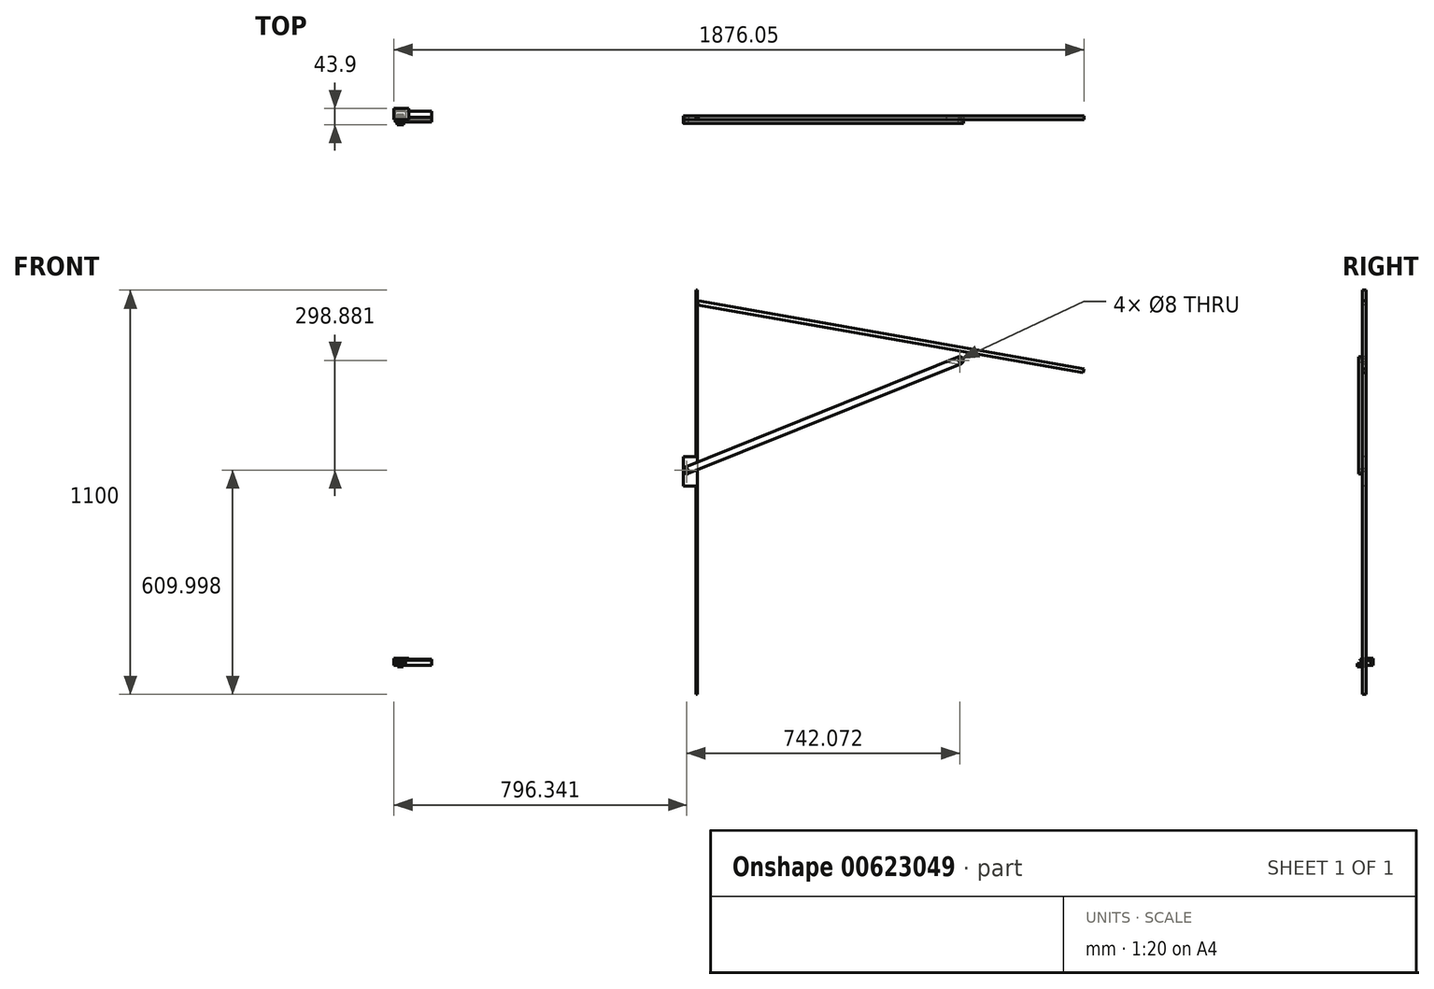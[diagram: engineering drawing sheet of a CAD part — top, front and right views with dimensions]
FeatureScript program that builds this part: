
annotation { "Feature Type Name" : "Feature", "Feature Type Description" : "" }
export const myFeature = defineFeature(function(context is Context, id is Id, definition is map)
    precondition{}
    {
        {
            var Q0;
            Q0=qCreatedBy(makeId("Front.planeOp"),FACE);
            var sketch = newSketch(context, id + "F0", { "sketchPlane" : qUnion([Q0])});
            skLineSegment(sketch, "E0.bottom", {"start": v(-1171.87, 12) * mm, "end": v(-1146.87, 12) * mm});
            skLineSegment(sketch, "E0.top", {"start": v(-1171.87, 0) * mm, "end": v(-1146.87, 0) * mm});
            skLineSegment(sketch, "E0.left", {"start": v(-1171.87, 12) * mm, "end": v(-1171.87, 0) * mm});
            skLineSegment(sketch, "E0.right", {"start": v(-1146.87, 12) * mm, "end": v(-1146.87, 0) * mm});
            skLineSegment(sketch, "E1.bottom", {"start": v(-1104.3, 0) * mm, "end": v(-1101.3, 0) * mm});
            skLineSegment(sketch, "E1.left", {"start": v(-1104.3, 0) * mm, "end": v(-1104.3, 20) * mm});
            skLineSegment(sketch, "E1.right", {"start": v(-1101.3, 0) * mm, "end": v(-1101.3, 17) * mm});
            skLineSegment(sketch, "E2.bottom", {"start": v(-1104.3, 20) * mm, "end": v(-1064.3, 20) * mm});
            skLineSegment(sketch, "E2.top", {"start": v(-1101.3, 17) * mm, "end": v(-1064.3, 17) * mm});
            skLineSegment(sketch, "E2.right", {"start": v(-1064.3, 20) * mm, "end": v(-1064.3, 17) * mm});
            skLineSegment(sketch, "E3.bottom", {"start": v(-1101.3, 17) * mm, "end": v(-1001.3, 17) * mm});
            skLineSegment(sketch, "E3.top", {"start": v(-1073.3, 0) * mm, "end": v(-1001.3, 0) * mm});
            skLineSegment(sketch, "E3.left", {"start": v(-1101.3, 17) * mm, "end": v(-1101.3, 9) * mm});
            skLineSegment(sketch, "E3.right", {"start": v(-1001.3, 17) * mm, "end": v(-1001.3, 0) * mm});
            skLineSegment(sketch, "E4", {"start": v(-1101.3, 15) * mm, "end": v(-1001.3, 15) * mm});
            skLineSegment(sketch, "E5", {"start": v(-1073.3, 0) * mm, "end": v(-1073.3, 9) * mm});
            skLineSegment(sketch, "E6", {"start": v(-1073.3, 9) * mm, "end": v(-1101.3, 9) * mm});
            skLineSegment(sketch, "E7.bottom", {"start": v(-1099.58, 0) * mm, "end": v(-1092.08, 0) * mm});
            skLineSegment(sketch, "E7.top", {"start": v(-1099.58, 9) * mm, "end": v(-1074.58, 9) * mm});
            skLineSegment(sketch, "E7.left", {"start": v(-1099.58, 0) * mm, "end": v(-1099.58, 9) * mm});
            skLineSegment(sketch, "E7.right", {"start": v(-1074.58, 0) * mm, "end": v(-1074.58, 9) * mm});
            skLineSegment(sketch, "E8", {"start": v(-1092.08, 0) * mm, "end": v(-1092.08, 2) * mm});
            skLineSegment(sketch, "E9", {"start": v(-1092.08, 2) * mm, "end": v(-1097.58, 2) * mm});
            skLineSegment(sketch, "E10", {"start": v(-1097.58, 2) * mm, "end": v(-1097.58, 7) * mm});
            skLineSegment(sketch, "E11", {"start": v(-1097.58, 7) * mm, "end": v(-1076.58, 7) * mm});
            skLineSegment(sketch, "E12", {"start": v(-1076.58, 7) * mm, "end": v(-1076.58, 2) * mm});
            skLineSegment(sketch, "E13", {"start": v(-1076.58, 2) * mm, "end": v(-1082.08, 2) * mm});
            skLineSegment(sketch, "E14", {"start": v(-1082.08, 2) * mm, "end": v(-1082.08, 0) * mm});
            skLineSegment(sketch, "E15.trimOffspring", {"start": v(-1082.08, 0) * mm, "end": v(-1074.58, 0) * mm});
            skLineSegment(sketch, "E16", {"start": v(-1094.68, -0.73) * mm, "end": v(-1094.68, -2.73) * mm});
            skLineSegment(sketch, "E17", {"start": v(-1094.68, -2.73) * mm, "end": v(-1079.68, -2.73) * mm});
            skLineSegment(sketch, "E18", {"start": v(-1079.68, -2.73) * mm, "end": v(-1079.68, -0.73) * mm});
            skLineSegment(sketch, "E19", {"start": v(-1079.68, -0.73) * mm, "end": v(-1083.18, -0.73) * mm});
            skLineSegment(sketch, "E20", {"start": v(-1083.18, -0.73) * mm, "end": v(-1083.18, 3.35) * mm});
            skLineSegment(sketch, "E21", {"start": v(-1083.18, 3.35) * mm, "end": v(-1077.87, 3.35) * mm});
            skLineSegment(sketch, "E22", {"start": v(-1077.87, 3.35) * mm, "end": v(-1077.87, 5.32) * mm});
            skLineSegment(sketch, "E23", {"start": v(-1077.87, 5.32) * mm, "end": v(-1096.5, 5.32) * mm});
            skLineSegment(sketch, "E24", {"start": v(-1096.5, 5.32) * mm, "end": v(-1096.5, 3.35) * mm});
            skLineSegment(sketch, "E25", {"start": v(-1096.5, 3.35) * mm, "end": v(-1091.18, 3.35) * mm});
            skLineSegment(sketch, "E26", {"start": v(-1091.18, 3.35) * mm, "end": v(-1091.18, -0.73) * mm});
            skLineSegment(sketch, "E27", {"start": v(-1091.18, -0.73) * mm, "end": v(-1094.68, -0.73) * mm});
            skLineSegment(sketch, "E28.bottom", {"start": v(-539.23, 1032.76) * mm, "end": v(-535.23, 1032.76) * mm});
            skLineSegment(sketch, "E28.top", {"start": v(-539.23, -67.24) * mm, "end": v(-535.23, -67.24) * mm});
            skLineSegment(sketch, "E28.left", {"start": v(-539.23, 1032.76) * mm, "end": v(-539.23, -67.24) * mm});
            skLineSegment(sketch, "E28.right", {"start": v(-535.23, 1032.76) * mm, "end": v(-535.23, -67.24) * mm});
            skLineSegment(sketch, "E29.left", {"start": v(-533.23, -72.18) * mm, "end": v(-533.23, 992.82) * mm});
            skLineSegment(sketch, "E29.right", {"start": v(-513.23, -72.18) * mm, "end": v(-513.23, 992.82) * mm});
            skLineSegment(sketch, "E30", {"start": v(-533.23, 992.82) * mm, "end": v(-513.23, 992.82) * mm});
            skLineSegment(sketch, "E31", {"start": v(-535.23, -47.24) * mm, "end": v(-539.23, -47.24) * mm});
            skLineSegment(sketch, "E32", {"start": v(-535.23, 992.82) * mm, "end": v(-539.23, 992.82) * mm});
            skLineSegment(sketch, "E33.bottom", {"start": v(-533.23, -72.18) * mm, "end": v(-513.23, -72.18) * mm});
            skLineSegment(sketch, "E33.top", {"start": v(-533.23, -32.18) * mm, "end": v(-513.23, -32.18) * mm});
            skLineSegment(sketch, "E33.left", {"start": v(-533.23, -72.18) * mm, "end": v(-533.23, -32.18) * mm});
            skLineSegment(sketch, "E33.right", {"start": v(-513.23, -72.18) * mm, "end": v(-513.23, -32.18) * mm});
            skLineSegment(sketch, "E34", {"start": v(-533.23, 952.82) * mm, "end": v(-513.23, 952.82) * mm});
            skLineSegment(sketch, "E35.bottom", {"start": v(-278.97, 1021.32) * mm, "end": v(-282.97, 1021.32) * mm});
            skLineSegment(sketch, "E35.top", {"start": v(-278.97, -78.68) * mm, "end": v(-282.97, -78.68) * mm});
            skLineSegment(sketch, "E35.left", {"start": v(-278.97, 1021.32) * mm, "end": v(-278.97, -78.68) * mm});
            skLineSegment(sketch, "E35.right", {"start": v(-282.97, 1021.32) * mm, "end": v(-282.97, -78.68) * mm});
            skLineSegment(sketch, "E36", {"start": v(-282.97, 981.32) * mm, "end": v(-278.97, 981.32) * mm});
            skLineSegment(sketch, "E37", {"start": v(-278.97, 981.32) * mm, "end": v(769.85, 796.38) * mm});
            skLineSegment(sketch, "E38", {"start": v(769.85, 796.38) * mm, "end": v(771.74, 807.12) * mm});
            skLineSegment(sketch, "E39", {"start": v(771.74, 807.12) * mm, "end": v(-277.08, 992.06) * mm});
            skLineSegment(sketch, "E40", {"start": v(-277.08, 992.06) * mm, "end": v(-278.97, 981.32) * mm});
            skLineSegment(sketch, "E41", {"start": v(-282.97, 531.32) * mm, "end": v(-278.97, 531.32) * mm});
            skLineSegment(sketch, "E42", {"start": v(432.47, -469.93) * mm, "end": v(1165.34, -599.16) * mm});
            skLineSegment(sketch, "E43", {"start": v(1165.34, -599.16) * mm, "end": v(432.47, -919.93) * mm});
            skLineSegment(sketch, "E44", {"start": v(432.47, -919.93) * mm, "end": v(432.47, -469.93) * mm});
            skCircle(sketch, "E45", {"center": v(-307.97, 531.32) * mm, "radius": 4 * mm});
            skLineSegment(sketch, "E46", {"start": v(-307.97, 531.32) * mm, "end": v(434.1, 830.2) * mm});
            skLineSegment(sketch, "E47.bottom", {"start": v(-282.97, 568.38) * mm, "end": v(-317.97, 568.38) * mm});
            skLineSegment(sketch, "E47.top", {"start": v(-282.97, 488.38) * mm, "end": v(-317.97, 488.38) * mm});
            skLineSegment(sketch, "E47.left", {"start": v(-282.97, 568.38) * mm, "end": v(-282.97, 488.38) * mm});
            skLineSegment(sketch, "E47.right", {"start": v(-317.97, 568.38) * mm, "end": v(-317.97, 488.38) * mm});
            skCircle(sketch, "E48", {"center": v(434.1, 830.2) * mm, "radius": 4 * mm});
            skArc(sketch, "E49.0.startCap", {"start": v(-304.23, 522.04) * mm, "mid": v(-317.25, 527.58) * mm, "end": v(-311.7, 540.6) * mm});
            skArc(sketch, "E49.0.endCap", {"start": v(430.37, 839.47) * mm, "mid": v(443.38, 833.93) * mm, "end": v(437.84, 820.92) * mm});
            skLineSegment(sketch, "E49.0.left", {"start": v(-311.7, 540.6) * mm, "end": v(430.37, 839.47) * mm});
            skLineSegment(sketch, "E49.0.right", {"start": v(-304.23, 522.04) * mm, "end": v(437.84, 820.92) * mm});
            skLineSegment(sketch, "E50", {"start": v(-282.97, 531.32) * mm, "end": v(-307.97, 531.32) * mm});
            skLineSegment(sketch, "E51", {"start": v(399.6, 861.67) * mm, "end": v(393.52, 827.2) * mm});
            skLineSegment(sketch, "E52", {"start": v(393.52, 827.2) * mm, "end": v(541.24, 801.15) * mm});
            skLineSegment(sketch, "E53", {"start": v(541.24, 801.15) * mm, "end": v(547.32, 835.62) * mm});
            skLineSegment(sketch, "E54.bottom", {"start": v(1672.22, 934.54) * mm, "end": v(1676.22, 934.54) * mm});
            skLineSegment(sketch, "E54.top", {"start": v(1672.22, -165.46) * mm, "end": v(1676.22, -165.46) * mm});
            skLineSegment(sketch, "E54.left", {"start": v(1672.22, 934.54) * mm, "end": v(1672.22, -165.46) * mm});
            skLineSegment(sketch, "E54.right", {"start": v(1676.22, 934.54) * mm, "end": v(1676.22, -165.46) * mm});
            skLineSegment(sketch, "E55", {"start": v(1676.22, 934.54) * mm, "end": v(2725.04, 749.6) * mm});
            skLineSegment(sketch, "E56", {"start": v(2437.6, 800.29) * mm, "end": v(2432.86, 775.74) * mm});
            skLineSegment(sketch, "E57", {"start": v(1647.22, 934.54) * mm, "end": v(1647.22, -165.46) * mm});
            skLineSegment(sketch, "E58", {"start": v(1676.22, 934.54) * mm, "end": v(1676.22, -130.46) * mm});
            skLineSegment(sketch, "E59", {"start": v(2432.86, 775.74) * mm, "end": v(1647.22, 637.22) * mm});
            skLineSegment(sketch, "E60", {"start": v(1646.05, 637.6) * mm, "end": v(1990.73, 698.37) * mm});
            skLineSegment(sketch, "E61", {"start": v(1989.57, 698.33) * mm, "end": v(2433.87, 776.68) * mm});
            skArc(sketch, "E62.0.startCap", {"start": v(1991.74, 686.02) * mm, "mid": v(1977.26, 696.16) * mm, "end": v(1987.4, 710.64) * mm});
            skArc(sketch, "E62.0.endCap", {"start": v(2431.7, 788.99) * mm, "mid": v(2446.18, 778.85) * mm, "end": v(2436.04, 764.37) * mm});
            skLineSegment(sketch, "E62.0.left", {"start": v(1987.4, 710.64) * mm, "end": v(2431.7, 788.99) * mm});
            skLineSegment(sketch, "E62.0.right", {"start": v(1991.74, 686.02) * mm, "end": v(2436.04, 764.37) * mm});
            skLineSegment(sketch, "E63.bottom", {"start": v(1306.32, 937.65) * mm, "end": v(1310.32, 937.65) * mm});
            skLineSegment(sketch, "E63.top", {"start": v(1306.32, -162.35) * mm, "end": v(1310.32, -162.35) * mm});
            skLineSegment(sketch, "E63.left", {"start": v(1306.32, 937.65) * mm, "end": v(1306.32, -162.35) * mm});
            skLineSegment(sketch, "E63.right", {"start": v(1310.32, 937.65) * mm, "end": v(1310.32, -162.35) * mm});
            skLineSegment(sketch, "E64.bottom", {"start": v(1310.32, 937.65) * mm, "end": v(1330.32, 937.65) * mm});
            skLineSegment(sketch, "E64.top", {"start": v(1310.32, -127.35) * mm, "end": v(1330.32, -127.35) * mm});
            skLineSegment(sketch, "E64.left", {"start": v(1310.32, 937.65) * mm, "end": v(1310.32, -127.35) * mm});
            skLineSegment(sketch, "E64.right", {"start": v(1330.32, 937.65) * mm, "end": v(1330.32, -127.35) * mm});
            skLineSegment(sketch, "E65", {"start": v(1281.32, 937.65) * mm, "end": v(1281.32, 640.65) * mm});
            skLineSegment(sketch, "E66", {"start": v(1281.32, 640.65) * mm, "end": v(1281.32, 190.65) * mm});
            skArc(sketch, "E67.0.startCap", {"start": v(1268.82, 640.65) * mm, "mid": v(1281.32, 653.15) * mm, "end": v(1293.82, 640.65) * mm});
            skArc(sketch, "E67.0.endCap", {"start": v(1293.82, 190.65) * mm, "mid": v(1281.32, 178.15) * mm, "end": v(1268.82, 190.65) * mm});
            skLineSegment(sketch, "E67.0.left", {"start": v(1293.82, 640.65) * mm, "end": v(1293.82, 190.65) * mm});
            skLineSegment(sketch, "E67.0.right", {"start": v(1268.82, 640.65) * mm, "end": v(1268.82, 190.65) * mm});
            skSolve(sketch);
        }
        {
            var Q0;
            {var subQ0=sQuery(id+"F0.wireOp",EDGE,"E35.bottom");Q0=makeQuery(id+"F0.imprint","IMPRINT",FACE,{"disambiguationData":[TD([[makeQuery(id+"F0.imprint","IMPRINT",EDGE,{"derivedFrom":subQ0}),1.0]])]});}
            var Q1;
            {var subQ0=sQuery(id+"F0.wireOp",EDGE,"E38");Q1=makeQuery(id+"F0.imprint","IMPRINT",FACE,{"disambiguationData":[TD([[makeQuery(id+"F0.imprint","IMPRINT",EDGE,{"derivedFrom":subQ0}),1.0]])]});}
            var Q2;
            {var subQ5=sQuery(id+"F0.wireOp",EDGE,"E36");Q2=makeQuery(id+"F0.imprint","IMPRINT",FACE,{"disambiguationData":[TD([[makeQuery(id+"F0.imprint","IMPRINT",EDGE,{"derivedFrom":subQ5}),-1.0]])]});}
            var Q3;
            {var subQ1=sQuery(id+"F0.wireOp",EDGE,"E49.0.endCap");Q3=makeQuery(id+"F0.imprint","IMPRINT",FACE,{"disambiguationData":[TD([[makeQuery(id+"F0.imprint","IMPRINT",EDGE,{"derivedFrom":subQ1}),1.0]])]});}
            var Q4;
            Q4=makeQuery(id+"F0.imprint","IMPRINT",FACE,{"disambiguationData":[TD([[makeQuery(id+"F0.imprint","IMPRINT",EDGE,{"derivedFrom":sQuery(id+"F0.wireOp",EDGE,"E48")}),-1.0]])]});
            var Q5;
            {var subQ5=sQuery(id+"F0.wireOp",EDGE,"E47.bottom");Q5=makeQuery(id+"F0.imprint","IMPRINT",FACE,{"disambiguationData":[TD([[makeQuery(id+"F0.imprint","IMPRINT",EDGE,{"derivedFrom":subQ5}),1.0]])]});}
            var Q6;
            {var subQ5=sQuery(id+"F0.wireOp",EDGE,"E47.top");Q6=makeQuery(id+"F0.imprint","IMPRINT",FACE,{"disambiguationData":[TD([[makeQuery(id+"F0.imprint","IMPRINT",EDGE,{"derivedFrom":subQ5}),-1.0]])]});}
            var Q7;
            {var subQ1=sQuery(id+"F0.wireOp",EDGE,"E46");var subQ5=sQuery(id+"F0.wireOp",EDGE,"E45");var subQ6=makeQuery(id+"F0.imprint","INTERSECT",VERTEX,{"derivedFrom":[subQ5,subQ1]});Q7=makeQuery(id+"F0.imprint","IMPRINT",FACE,{"disambiguationData":[TD([[makeQuery(id+"F0.imprint","IMPRINT",EDGE,{"disambiguationData":[TD([[subQ6,-1.0]])],"derivedFrom":subQ5}),-1.0]])]});}
            var Q8;
            {var subQ0=sQuery(id+"F0.wireOp",EDGE,"E46");var subQ1=sQuery(id+"F0.wireOp",EDGE,"E45");var subQ2=makeQuery(id+"F0.imprint","INTERSECT",VERTEX,{"derivedFrom":[subQ1,subQ0]});Q8=makeQuery(id+"F0.imprint","IMPRINT",FACE,{"disambiguationData":[TD([[makeQuery(id+"F0.imprint","IMPRINT",EDGE,{"disambiguationData":[TD([[subQ2,1.0]])],"derivedFrom":subQ1}),-1.0]])]});}
            var Q9;
            {var subQ1=sQuery(id+"F0.wireOp",EDGE,"E41");var subQ3=sQuery(id+"F0.wireOp",EDGE,"E49.0.right");var subQ4=makeQuery(id+"F0.imprint","INTERSECT",VERTEX,{"derivedFrom":[subQ1,subQ3]});Q9=makeQuery(id+"F0.imprint","IMPRINT",FACE,{"disambiguationData":[TD([[makeQuery(id+"F0.imprint","IMPRINT",EDGE,{"disambiguationData":[TD([[subQ4,1.0]])],"derivedFrom":subQ3}),1.0]])]});}
            var Q10;
            {var subQ0=sQuery(id+"F0.wireOp",EDGE,"E41");var subQ1=sQuery(id+"F0.wireOp",EDGE,"E35.left");var subQ2=makeQuery(id+"F0.imprint","INTERSECT",VERTEX,{"derivedFrom":[subQ1,subQ0]});Q10=makeQuery(id+"F0.imprint","IMPRINT",FACE,{"disambiguationData":[TD([[makeQuery(id+"F0.imprint","IMPRINT",EDGE,{"disambiguationData":[TD([[subQ2,1.0]])],"derivedFrom":subQ1}),-1.0]])]});}
            var Q11;
            {var subQ1=sQuery(id+"F0.wireOp",EDGE,"E35.left");var subQ5=sQuery(id+"F0.wireOp",EDGE,"E49.0.right");var subQ6=makeQuery(id+"F0.imprint","INTERSECT",VERTEX,{"derivedFrom":[subQ1,subQ5]});Q11=makeQuery(id+"F0.imprint","IMPRINT",FACE,{"disambiguationData":[TD([[makeQuery(id+"F0.imprint","IMPRINT",EDGE,{"disambiguationData":[TD([[subQ6,1.0]])],"derivedFrom":subQ1}),-1.0]])]});}
            var Q12;
            {var subQ0=sQuery(id+"F0.wireOp",EDGE,"E49.0.left");var subQ1=sQuery(id+"F0.wireOp",EDGE,"E35.left");var subQ2=makeQuery(id+"F0.imprint","INTERSECT",VERTEX,{"derivedFrom":[subQ1,subQ0]});Q12=makeQuery(id+"F0.imprint","IMPRINT",FACE,{"disambiguationData":[TD([[makeQuery(id+"F0.imprint","IMPRINT",EDGE,{"disambiguationData":[TD([[subQ2,-1.0]])],"derivedFrom":subQ1}),-1.0]])]});}
            var Q13;
            {var subQ6=sQuery(id+"F0.wireOp",EDGE,"E35.top");Q13=makeQuery(id+"F0.imprint","IMPRINT",FACE,{"disambiguationData":[TD([[makeQuery(id+"F0.imprint","IMPRINT",EDGE,{"derivedFrom":subQ6}),-1.0]])]});}
            extrude(context, id + "F1", {"entities" : qUnion([Q0, Q1, Q2, Q3, Q4, Q5, Q6, Q7, Q8, Q9, Q10, Q11, Q12, Q13]), "oppositeDirection" : true, "depth" : 10 * mm, "offsetDistance" : 25 * mm});
        }
        {
            var Q0;
            {var subQ1=sQuery(id+"F0.wireOp",EDGE,"E46");var subQ5=sQuery(id+"F0.wireOp",EDGE,"E45");var subQ6=makeQuery(id+"F0.imprint","INTERSECT",VERTEX,{"derivedFrom":[subQ5,subQ1]});Q0=makeQuery(id+"F0.imprint","IMPRINT",FACE,{"disambiguationData":[TD([[makeQuery(id+"F0.imprint","IMPRINT",EDGE,{"disambiguationData":[TD([[subQ6,-1.0]])],"derivedFrom":subQ5}),-1.0]])]});}
            var Q1;
            {var subQ0=sQuery(id+"F0.wireOp",EDGE,"E49.0.left");var subQ1=sQuery(id+"F0.wireOp",EDGE,"E35.left");var subQ2=makeQuery(id+"F0.imprint","INTERSECT",VERTEX,{"derivedFrom":[subQ1,subQ0]});Q1=makeQuery(id+"F0.imprint","IMPRINT",FACE,{"disambiguationData":[TD([[makeQuery(id+"F0.imprint","IMPRINT",EDGE,{"disambiguationData":[TD([[subQ2,-1.0]])],"derivedFrom":subQ1}),-1.0]])]});}
            var Q2;
            {var subQ0=sQuery(id+"F0.wireOp",EDGE,"E46");var subQ1=sQuery(id+"F0.wireOp",EDGE,"E45");var subQ2=makeQuery(id+"F0.imprint","INTERSECT",VERTEX,{"derivedFrom":[subQ1,subQ0]});Q2=makeQuery(id+"F0.imprint","IMPRINT",FACE,{"disambiguationData":[TD([[makeQuery(id+"F0.imprint","IMPRINT",EDGE,{"disambiguationData":[TD([[subQ2,1.0]])],"derivedFrom":subQ1}),-1.0]])]});}
            var Q3;
            {var subQ1=sQuery(id+"F0.wireOp",EDGE,"E35.left");var subQ5=sQuery(id+"F0.wireOp",EDGE,"E49.0.right");var subQ6=makeQuery(id+"F0.imprint","INTERSECT",VERTEX,{"derivedFrom":[subQ1,subQ5]});Q3=makeQuery(id+"F0.imprint","IMPRINT",FACE,{"disambiguationData":[TD([[makeQuery(id+"F0.imprint","IMPRINT",EDGE,{"disambiguationData":[TD([[subQ6,1.0]])],"derivedFrom":subQ1}),-1.0]])]});}
            var Q4;
            {var subQ1=sQuery(id+"F0.wireOp",EDGE,"E41");var subQ3=sQuery(id+"F0.wireOp",EDGE,"E49.0.right");var subQ4=makeQuery(id+"F0.imprint","INTERSECT",VERTEX,{"derivedFrom":[subQ1,subQ3]});Q4=makeQuery(id+"F0.imprint","IMPRINT",FACE,{"disambiguationData":[TD([[makeQuery(id+"F0.imprint","IMPRINT",EDGE,{"disambiguationData":[TD([[subQ4,1.0]])],"derivedFrom":subQ3}),1.0]])]});}
            var Q5;
            {var subQ0=sQuery(id+"F0.wireOp",EDGE,"E49.0.left");var subQ1=sQuery(id+"F0.wireOp",EDGE,"E35.left");var subQ2=makeQuery(id+"F0.imprint","INTERSECT",VERTEX,{"derivedFrom":[subQ1,subQ0]});Q5=makeQuery(id+"F0.imprint","IMPRINT",FACE,{"disambiguationData":[TD([[makeQuery(id+"F0.imprint","IMPRINT",EDGE,{"disambiguationData":[TD([[subQ2,-1.0]])],"derivedFrom":subQ1}),1.0]])]});}
            var Q6;
            {var subQ0=sQuery(id+"F0.wireOp",EDGE,"E49.0.right");var subQ1=sQuery(id+"F0.wireOp",EDGE,"E35.left");var subQ2=makeQuery(id+"F0.imprint","INTERSECT",VERTEX,{"derivedFrom":[subQ1,subQ0]});Q6=makeQuery(id+"F0.imprint","IMPRINT",FACE,{"disambiguationData":[TD([[makeQuery(id+"F0.imprint","IMPRINT",EDGE,{"disambiguationData":[TD([[subQ2,1.0]])],"derivedFrom":subQ1}),1.0]])]});}
            var Q7;
            Q7=makeQuery(id+"F0.imprint","IMPRINT",FACE,{"disambiguationData":[TD([[makeQuery(id+"F0.imprint","IMPRINT",EDGE,{"derivedFrom":sQuery(id+"F0.wireOp",EDGE,"E48")}),-1.0]])]});
            extrude(context, id + "F2", {"entities" : qUnion([Q0, Q1, Q2, Q3, Q4, Q5, Q6, Q7]), "depth" : 10 * mm, "offsetDistance" : 25 * mm});
        }
        {
            var Q0;
            Q0=makeQuery(id+"F0.imprint","IMPRINT",FACE,{"disambiguationData":[TD([[makeQuery(id+"F0.imprint","IMPRINT",EDGE,{"derivedFrom":sQuery(id+"F0.wireOp",EDGE,"E1.bottom")}),1.0]])]});
            extrude(context, id + "F3", {"entities" : qUnion([Q0]), "oppositeDirection" : true, "depth" : 30 * mm, "offsetDistance" : 25 * mm});
        }
        {
            var Q0;
            {var subQ1=sQuery(id+"F0.wireOp",EDGE,"E3.top");Q0=makeQuery(id+"F0.imprint","IMPRINT",FACE,{"disambiguationData":[TD([[makeQuery(id+"F0.imprint","IMPRINT",EDGE,{"derivedFrom":subQ1}),1.0]])]});}
            extrude(context, id + "F4", {"entities" : qUnion([Q0]), "oppositeDirection" : true, "depth" : 22.8 * mm, "offsetDistance" : 25 * mm});
        }
        {
            var Q0;
            {var subQ3=sQuery(id+"F0.wireOp",EDGE,"E4");Q0=makeQuery(id+"F0.imprint","IMPRINT",FACE,{"disambiguationData":[TD([[makeQuery(id+"F0.imprint","IMPRINT",EDGE,{"derivedFrom":subQ3}),1.0]])]});}
            extrude(context, id + "F5", {"entities" : qUnion([Q0]), "endBound" : BoundingType.SYMMETRIC, "oppositeDirection" : true, "depth" : 12.4 * mm, "offsetDistance" : 25 * mm});
        }
        {
            var Q0;
            Q0=makeQuery(id+"F0.imprint","IMPRINT",FACE,{"disambiguationData":[TD([[makeQuery(id+"F0.imprint","IMPRINT",EDGE,{"derivedFrom":sQuery(id+"F0.wireOp",EDGE,"E7.bottom")}),1.0]])]});
            extrude(context, id + "F6", {"entities" : qUnion([Q0]), "operationType" : NewBodyOperationType.ADD, "endBound" : BoundingType.SYMMETRIC, "depth" : 15.6 * mm, "offsetDistance" : 25 * mm});
        }
        {
            var Q0;
            Q0=makeQuery(id+"F0.imprint","IMPRINT",FACE,{"disambiguationData":[TD([[makeQuery(id+"F0.imprint","IMPRINT",EDGE,{"derivedFrom":sQuery(id+"F0.wireOp",EDGE,"E16")}),1.0]])]});
            extrude(context, id + "F7", {"entities" : qUnion([Q0]), "endBound" : BoundingType.SYMMETRIC, "depth" : 27.8 * mm, "offsetDistance" : 25 * mm});
        }
    });
